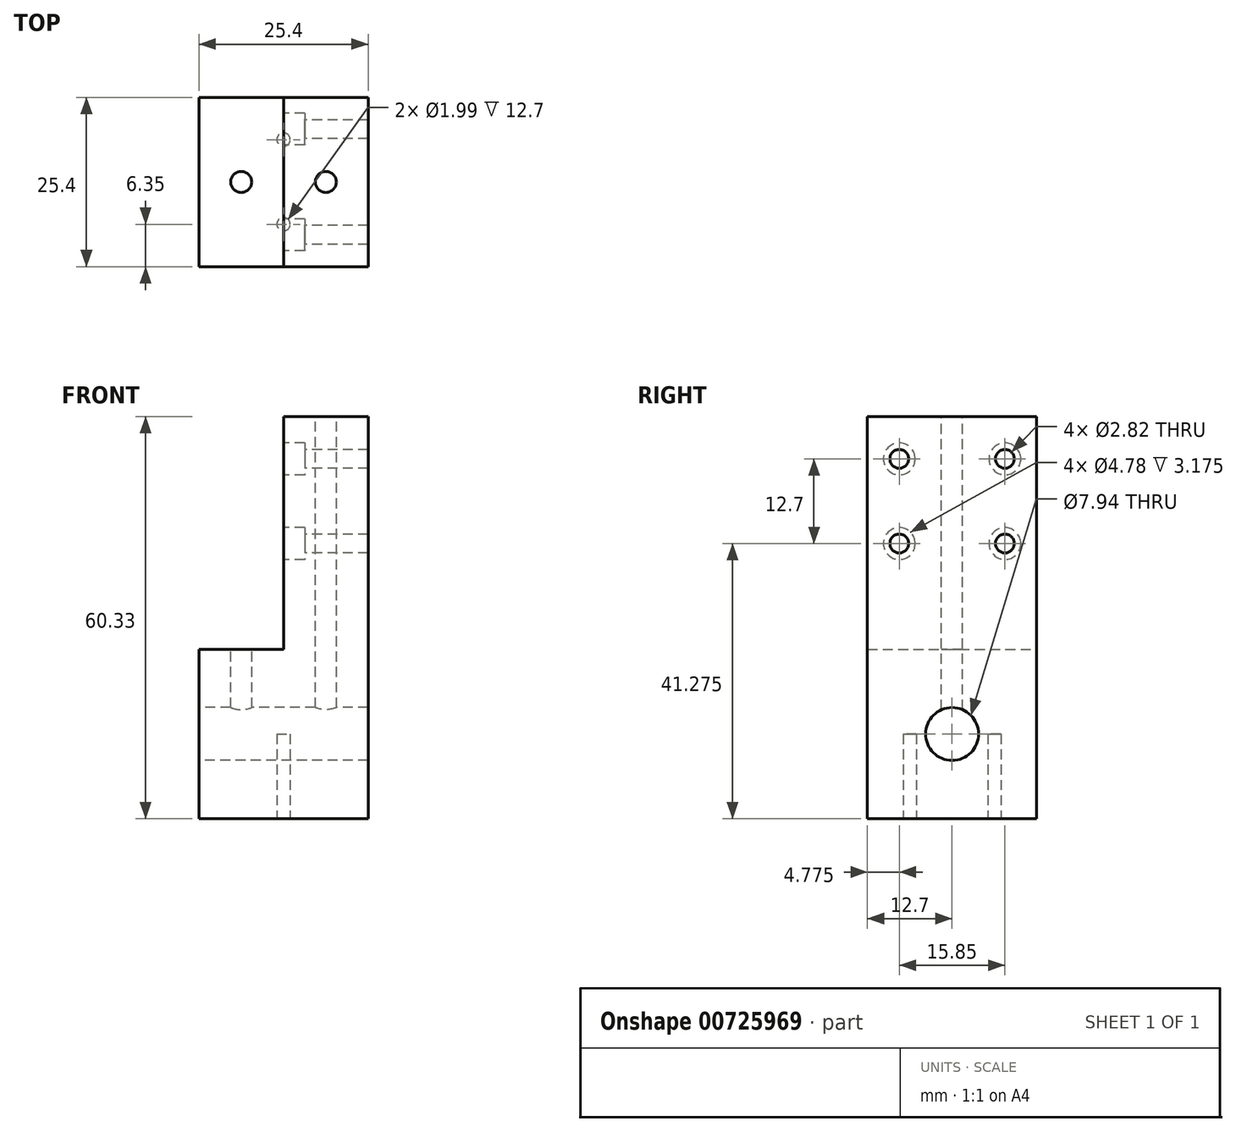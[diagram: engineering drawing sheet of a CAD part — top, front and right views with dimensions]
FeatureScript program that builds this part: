
annotation { "Feature Type Name" : "Feature", "Feature Type Description" : "" }
export const myFeature = defineFeature(function(context is Context, id is Id, definition is map)
    precondition{}
    {
        {
            var Q0;
            Q0=qCreatedBy(makeId("Front.planeOp"),FACE);
            var sketch = newSketch(context, id + "F0", { "sketchPlane" : qUnion([Q0])});
            skLineSegment(sketch, "E0.bottom", {"start": v(0, 0) * mm, "end": v(25.4, 0) * mm});
            skLineSegment(sketch, "E0.top", {"start": v(0, 25.4) * mm, "end": v(12.7, 25.4) * mm});
            skLineSegment(sketch, "E0.left", {"start": v(0, 0) * mm, "end": v(0, 25.4) * mm});
            skLineSegment(sketch, "E1.top", {"start": v(12.7, 60.33) * mm, "end": v(25.4, 60.33) * mm});
            skLineSegment(sketch, "E1.left", {"start": v(12.7, 25.4) * mm, "end": v(12.7, 60.33) * mm});
            skLineSegment(sketch, "E2", {"start": v(25.4, 60.33) * mm, "end": v(25.4, 0) * mm});
            skSolve(sketch);
        }
        {
            var Q0;
            Q0 = qSketchRegion(id + "F0", true);
            extrude(context, id + "F1", {"entities" : qUnion([Q0]), "depth" : 25.4 * mm, "offsetDistance" : 25.4 * mm});
        }
        {
            var Q0;
            Q0=makeQuery(id+"F1.opExtrude","SWEPT_FACE",FACE,{"disambiguationData":[OSD([sQuery(id+"F0.wireOp",EDGE,"E1.top")])]});
            var sketch = newSketch(context, id + "F2", { "sketchPlane" : qUnion([Q0])});
            skCircle(sketch, "E3", {"center": v(19.05, -12.7) * mm, "radius": 1.59 * mm});
            skSolve(sketch);
        }
        {
            var Q0;
            Q0 = qSketchRegion(id + "F2", true);
            extrude(context, id + "F3", {"entities" : qUnion([Q0]), "operationType" : NewBodyOperationType.REMOVE, "oppositeDirection" : true, "depth" : 49.02 * mm, "offsetDistance" : 25.4 * mm});
        }
        {
            var Q0;
            Q0=makeQuery(id+"F1.opExtrude","SWEPT_FACE",FACE,{"disambiguationData":[OSD([sQuery(id+"F0.wireOp",EDGE,"E0.left")])]});
            var sketch = newSketch(context, id + "F4", { "sketchPlane" : qUnion([Q0])});
            skCircle(sketch, "E4", {"center": v(12.7, 12.7) * mm, "radius": 3.97 * mm});
            skSolve(sketch);
        }
        {
            var Q0;
            Q0 = qSketchRegion(id + "F4", true);
            extrude(context, id + "F5", {"entities" : qUnion([Q0]), "operationType" : NewBodyOperationType.REMOVE, "oppositeDirection" : true, "depth" : 25.4 * mm, "offsetDistance" : 25.4 * mm});
        }
        {
            var Q0;
            Q0=makeQuery(id+"F1.opExtrude","SWEPT_FACE",FACE,{"disambiguationData":[OSD([sQuery(id+"F0.wireOp",EDGE,"E1.left")])]});
            var sketch = newSketch(context, id + "F6", { "sketchPlane" : qUnion([Q0])});
            skCircle(sketch, "E5", {"center": v(4.78, 53.98) * mm, "radius": 1.4 * mm});
            skCircle(sketch, "E6", {"center": v(4.78, 41.27) * mm, "radius": 1.4 * mm});
            skCircle(sketch, "E7", {"center": v(20.62, 53.98) * mm, "radius": 1.4 * mm});
            skCircle(sketch, "E8", {"center": v(20.62, 41.27) * mm, "radius": 1.4 * mm});
            skSolve(sketch);
        }
        {
            var Q0;
            Q0 = qSketchRegion(id + "F6", true);
            extrude(context, id + "F7", {"entities" : qUnion([Q0]), "operationType" : NewBodyOperationType.REMOVE, "oppositeDirection" : true, "depth" : 25.4 * mm, "offsetDistance" : 25.4 * mm});
        }
        {
            var Q0;
            Q0=makeQuery(id+"F1.opExtrude","SWEPT_FACE",FACE,{"disambiguationData":[OSD([sQuery(id+"F0.wireOp",EDGE,"E1.left")])]});
            var sketch = newSketch(context, id + "F8", { "sketchPlane" : qUnion([Q0])});
            skSolve(sketch);
        }
        {
            var Q0;
            {var subQ0=sQuery(id+"F0.wireOp",EDGE,"E1.left");Q0=makeQuery(id+"F8.imprint","IMPRINT",FACE,{"disambiguationData":[TD([[makeQuery(id+"F8.imprint","IMPRINT",EDGE,{"derivedFrom":makeQuery(id+"F1.opExtrude","CAP_EDGE",EDGE,{"disambiguationData":[OSD([subQ0])],"isStart":true})}),-1.0]])]});}
            var sketch = newSketch(context, id + "F9", { "sketchPlane" : qUnion([Q0])});
            skCircle(sketch, "E9", {"center": v(4.78, 53.98) * mm, "radius": 2.39 * mm});
            skCircle(sketch, "E10", {"center": v(4.78, 41.27) * mm, "radius": 2.39 * mm});
            skCircle(sketch, "E11", {"center": v(20.62, 41.27) * mm, "radius": 2.39 * mm});
            skCircle(sketch, "E12", {"center": v(20.62, 53.98) * mm, "radius": 2.39 * mm});
            skSolve(sketch);
        }
        {
            var Q0;
            Q0 = qSketchRegion(id + "F9", true);
            extrude(context, id + "F10", {"entities" : qUnion([Q0]), "operationType" : NewBodyOperationType.REMOVE, "oppositeDirection" : true, "depth" : 3.17 * mm, "offsetDistance" : 25.4 * mm});
        }
        {
            var Q0;
            Q0=makeQuery(id+"F1.opExtrude","SWEPT_FACE",FACE,{"disambiguationData":[OSD([sQuery(id+"F0.wireOp",EDGE,"E0.bottom")])]});
            var sketch = newSketch(context, id + "F11", { "sketchPlane" : qUnion([Q0])});
            skCircle(sketch, "E13", {"center": v(12.7, 19.05) * mm, "radius": 1 * mm});
            skCircle(sketch, "E14", {"center": v(12.7, 6.35) * mm, "radius": 1 * mm});
            skSolve(sketch);
        }
        {
            var Q0;
            Q0 = qSketchRegion(id + "F11", true);
            extrude(context, id + "F12", {"entities" : qUnion([Q0]), "operationType" : NewBodyOperationType.REMOVE, "oppositeDirection" : true, "depth" : 12.7 * mm, "offsetDistance" : 25.4 * mm});
        }
        {
            var Q0;
            Q0=makeQuery(id+"F1.opExtrude","SWEPT_FACE",FACE,{"disambiguationData":[OSD([sQuery(id+"F0.wireOp",EDGE,"E0.top")])]});
            var sketch = newSketch(context, id + "F13", { "sketchPlane" : qUnion([Q0])});
            skCircle(sketch, "E15", {"center": v(6.35, -12.7) * mm, "radius": 1.59 * mm});
            skSolve(sketch);
        }
        {
            var Q0;
            Q0 = qSketchRegion(id + "F13", true);
            extrude(context, id + "F14", {"entities" : qUnion([Q0]), "operationType" : NewBodyOperationType.REMOVE, "oppositeDirection" : true, "depth" : 13.72 * mm, "offsetDistance" : 25.4 * mm});
        }
    });
